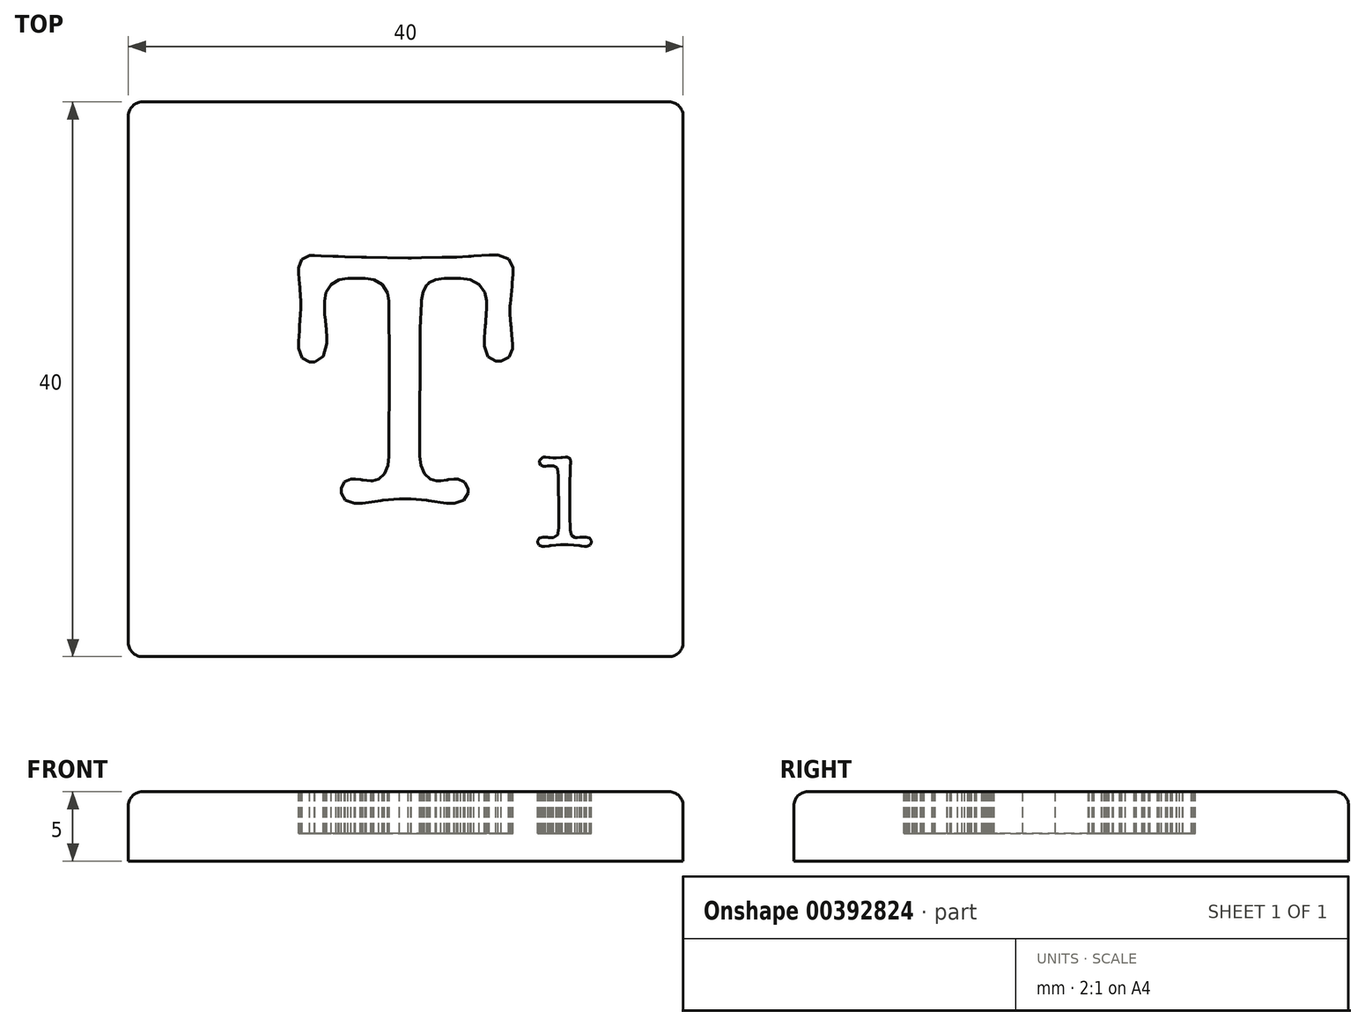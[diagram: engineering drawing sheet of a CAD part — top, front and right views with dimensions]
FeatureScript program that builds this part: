
annotation { "Feature Type Name" : "Feature", "Feature Type Description" : "" }
export const myFeature = defineFeature(function(context is Context, id is Id, definition is map)
    precondition{}
    {
        {
            var Q0;
            Q0=qCreatedBy(makeId("Top.planeOp"),FACE);
            var sketch = newSketch(context, id + "F0", { "sketchPlane" : qUnion([Q0])});
            skLineSegment(sketch, "E0.bottom", {"start": v(20, -20) * mm, "end": v(-20, -20) * mm});
            skLineSegment(sketch, "E0.top", {"start": v(20, 20) * mm, "end": v(-20, 20) * mm});
            skLineSegment(sketch, "E0.left", {"start": v(20, -20) * mm, "end": v(20, 20) * mm});
            skLineSegment(sketch, "E0.right", {"start": v(-20, -20) * mm, "end": v(-20, 20) * mm});
            skPoint(sketch, "E0.middle", {"position": v(0, 0) * mm});
            skSolve(sketch);
        }
        {
            var Q0;
            Q0=makeQuery(id+"F0.imprint","IMPRINT",FACE,{"disambiguationData":[TD([[makeQuery(id+"F0.imprint","IMPRINT",EDGE,{"derivedFrom":sQuery(id+"F0.wireOp",EDGE,"E0.bottom")}),-1.0]])]});
            extrude(context, id + "F1", {"entities" : qUnion([Q0]), "flatOperationType" : FlatOperationType.REMOVE, "offsetDistance" : 25 * mm, "depth" : -5 * mm, "domain" : OperationDomain.MODEL});
        }
        {
            var Q0;
            Q0=makeQuery(id+"F1.opExtrude","CAP_FACE",FACE,{"disambiguationData":[OSD([sQuery(id+"F0.wireOp",EDGE,"E0.bottom"),sQuery(id+"F0.wireOp",EDGE,"E0.top"),sQuery(id+"F0.wireOp",EDGE,"E0.left"),sQuery(id+"F0.wireOp",EDGE,"E0.right")])],"isStart":true});
            var Q1;
            Q1=makeQuery(id+"F1.opExtrude","SWEPT_EDGE",EDGE,{"disambiguationData":[OSD([sQuery(id+"F0.wireOp",EDGE,"E0.top"),sQuery(id+"F0.wireOp",EDGE,"E0.right")])]});
            var Q2;
            Q2=makeQuery(id+"F1.opExtrude","SWEPT_EDGE",EDGE,{"disambiguationData":[OSD([sQuery(id+"F0.wireOp",EDGE,"E0.top"),sQuery(id+"F0.wireOp",EDGE,"E0.left")])]});
            var Q3;
            Q3=makeQuery(id+"F1.opExtrude","SWEPT_EDGE",EDGE,{"disambiguationData":[OSD([sQuery(id+"F0.wireOp",EDGE,"E0.bottom"),sQuery(id+"F0.wireOp",EDGE,"E0.right")])]});
            var Q4;
            Q4=makeQuery(id+"F1.opExtrude","SWEPT_EDGE",EDGE,{"disambiguationData":[OSD([sQuery(id+"F0.wireOp",EDGE,"E0.bottom"),sQuery(id+"F0.wireOp",EDGE,"E0.left")])]});
            fillet(context, id + "F2", {"entities" : qUnion([Q0, Q1, Q2, Q3, Q4]), "radius" : 1 * mm, "tangentPropagation" : true, "allowEdgeOverflow" : false});
        }
        {
            var Q0;
            Q0=qCreatedBy(makeId("Top.planeOp"),FACE);
            var sketch = newSketch(context, id + "F3", { "sketchPlane" : qUnion([Q0])});
            skLineSegment(sketch, "E1", {"start": v(1.02, -5.33) * mm, "end": v(1.02, -5.55) * mm});
            skLineSegment(sketch, "E2", {"start": v(1.02, -5.55) * mm, "end": v(1.1, -6.2) * mm});
            skLineSegment(sketch, "E3", {"start": v(1.1, -6.2) * mm, "end": v(1.36, -6.82) * mm});
            skLineSegment(sketch, "E4", {"start": v(1.36, -6.82) * mm, "end": v(1.78, -7.2) * mm});
            skLineSegment(sketch, "E5", {"start": v(1.78, -7.2) * mm, "end": v(2.22, -7.32) * mm});
            skLineSegment(sketch, "E6", {"start": v(2.22, -7.32) * mm, "end": v(2.37, -7.32) * mm});
            skLineSegment(sketch, "E7", {"start": v(2.37, -7.32) * mm, "end": v(2.53, -7.32) * mm});
            skLineSegment(sketch, "E8", {"start": v(2.53, -7.32) * mm, "end": v(2.93, -7.26) * mm});
            skLineSegment(sketch, "E9", {"start": v(2.93, -7.26) * mm, "end": v(3, -7.25) * mm});
            skLineSegment(sketch, "E10", {"start": v(3, -7.25) * mm, "end": v(3.07, -7.24) * mm});
            skLineSegment(sketch, "E11", {"start": v(3.07, -7.24) * mm, "end": v(3.5, -7.18) * mm});
            skLineSegment(sketch, "E12", {"start": v(3.5, -7.18) * mm, "end": v(3.64, -7.18) * mm});
            skLineSegment(sketch, "E13", {"start": v(3.64, -7.18) * mm, "end": v(3.79, -7.18) * mm});
            skLineSegment(sketch, "E14", {"start": v(3.79, -7.18) * mm, "end": v(4.2, -7.4) * mm});
            skLineSegment(sketch, "E15", {"start": v(4.2, -7.4) * mm, "end": v(4.23, -7.43) * mm});
            skLineSegment(sketch, "E16", {"start": v(4.23, -7.43) * mm, "end": v(4.27, -7.48) * mm});
            skLineSegment(sketch, "E17", {"start": v(4.27, -7.48) * mm, "end": v(4.49, -7.9) * mm});
            skLineSegment(sketch, "E18", {"start": v(4.49, -7.9) * mm, "end": v(4.49, -8.03) * mm});
            skLineSegment(sketch, "E19", {"start": v(4.49, -8.03) * mm, "end": v(4.49, -8.2) * mm});
            skLineSegment(sketch, "E20", {"start": v(4.49, -8.2) * mm, "end": v(4.19, -8.72) * mm});
            skLineSegment(sketch, "E21", {"start": v(4.19, -8.72) * mm, "end": v(3.52, -8.96) * mm});
            skLineSegment(sketch, "E22", {"start": v(3.52, -8.96) * mm, "end": v(3.3, -8.96) * mm});
            skLineSegment(sketch, "E23", {"start": v(3.3, -8.96) * mm, "end": v(3.14, -8.96) * mm});
            skLineSegment(sketch, "E24", {"start": v(3.14, -8.96) * mm, "end": v(3.11, -8.95) * mm});
            skLineSegment(sketch, "E25", {"start": v(3.11, -8.95) * mm, "end": v(3, -8.93) * mm});
            skLineSegment(sketch, "E26", {"start": v(3, -8.93) * mm, "end": v(2.95, -8.93) * mm});
            skLineSegment(sketch, "E27", {"start": v(2.95, -8.93) * mm, "end": v(1.65, -8.74) * mm});
            skLineSegment(sketch, "E28", {"start": v(1.65, -8.74) * mm, "end": v(1.53, -8.73) * mm});
            skLineSegment(sketch, "E29", {"start": v(1.53, -8.73) * mm, "end": v(0.37, -8.64) * mm});
            skLineSegment(sketch, "E30", {"start": v(0.37, -8.64) * mm, "end": v(-0.01, -8.64) * mm});
            skLineSegment(sketch, "E31", {"start": v(-0.01, -8.64) * mm, "end": v(-0.46, -8.64) * mm});
            skLineSegment(sketch, "E32", {"start": v(-0.46, -8.64) * mm, "end": v(-1.66, -8.73) * mm});
            skLineSegment(sketch, "E33", {"start": v(-1.66, -8.73) * mm, "end": v(-1.79, -8.74) * mm});
            skLineSegment(sketch, "E34", {"start": v(-1.79, -8.74) * mm, "end": v(-3.1, -8.93) * mm});
            skLineSegment(sketch, "E35", {"start": v(-3.1, -8.93) * mm, "end": v(-3.16, -8.93) * mm});
            skLineSegment(sketch, "E36", {"start": v(-3.16, -8.93) * mm, "end": v(-3.28, -8.95) * mm});
            skLineSegment(sketch, "E37", {"start": v(-3.28, -8.95) * mm, "end": v(-3.3, -8.96) * mm});
            skLineSegment(sketch, "E38", {"start": v(-3.3, -8.96) * mm, "end": v(-3.48, -8.96) * mm});
            skLineSegment(sketch, "E39", {"start": v(-3.48, -8.96) * mm, "end": v(-3.7, -8.96) * mm});
            skLineSegment(sketch, "E40", {"start": v(-3.7, -8.96) * mm, "end": v(-4.35, -8.72) * mm});
            skLineSegment(sketch, "E41", {"start": v(-4.35, -8.72) * mm, "end": v(-4.64, -8.2) * mm});
            skLineSegment(sketch, "E42", {"start": v(-4.64, -8.2) * mm, "end": v(-4.64, -8.03) * mm});
            skLineSegment(sketch, "E43", {"start": v(-4.64, -8.03) * mm, "end": v(-4.64, -7.87) * mm});
            skLineSegment(sketch, "E44", {"start": v(-4.64, -7.87) * mm, "end": v(-4.43, -7.4) * mm});
            skLineSegment(sketch, "E45", {"start": v(-4.43, -7.4) * mm, "end": v(-3.96, -7.18) * mm});
            skLineSegment(sketch, "E46", {"start": v(-3.96, -7.18) * mm, "end": v(-3.8, -7.18) * mm});
            skLineSegment(sketch, "E47", {"start": v(-3.8, -7.18) * mm, "end": v(-3.64, -7.18) * mm});
            skLineSegment(sketch, "E48", {"start": v(-3.64, -7.18) * mm, "end": v(-3.23, -7.24) * mm});
            skLineSegment(sketch, "E49", {"start": v(-3.23, -7.24) * mm, "end": v(-3.16, -7.25) * mm});
            skLineSegment(sketch, "E50", {"start": v(-3.16, -7.25) * mm, "end": v(-3.1, -7.26) * mm});
            skLineSegment(sketch, "E51", {"start": v(-3.1, -7.26) * mm, "end": v(-2.53, -7.32) * mm});
            skLineSegment(sketch, "E52", {"start": v(-2.53, -7.32) * mm, "end": v(-2.38, -7.32) * mm});
            skLineSegment(sketch, "E53", {"start": v(-2.38, -7.32) * mm, "end": v(-1.95, -7.2) * mm});
            skLineSegment(sketch, "E54", {"start": v(-1.95, -7.2) * mm, "end": v(-1.53, -6.82) * mm});
            skLineSegment(sketch, "E55", {"start": v(-1.53, -6.82) * mm, "end": v(-1.29, -6.2) * mm});
            skLineSegment(sketch, "E56", {"start": v(-1.29, -6.2) * mm, "end": v(-1.2, -5.55) * mm});
            skLineSegment(sketch, "E57", {"start": v(-1.2, -5.55) * mm, "end": v(-1.2, -5.33) * mm});
            skLineSegment(sketch, "E58", {"start": v(-1.2, -5.33) * mm, "end": v(-1.2, -3.48) * mm});
            skLineSegment(sketch, "E59", {"start": v(-1.2, -3.48) * mm, "end": v(-1.18, -1.15) * mm});
            skLineSegment(sketch, "E60", {"start": v(-1.18, -1.15) * mm, "end": v(-1.18, 1.1) * mm});
            skLineSegment(sketch, "E61", {"start": v(-1.18, 1.1) * mm, "end": v(-1.2, 5.41) * mm});
            skLineSegment(sketch, "E62", {"start": v(-1.2, 5.41) * mm, "end": v(-1.2, 5.62) * mm});
            skLineSegment(sketch, "E63", {"start": v(-1.2, 5.62) * mm, "end": v(-1.32, 6.23) * mm});
            skLineSegment(sketch, "E64", {"start": v(-1.32, 6.23) * mm, "end": v(-1.69, 6.82) * mm});
            skLineSegment(sketch, "E65", {"start": v(-1.69, 6.82) * mm, "end": v(-2.3, 7.17) * mm});
            skLineSegment(sketch, "E66", {"start": v(-2.3, 7.17) * mm, "end": v(-2.92, 7.29) * mm});
            skLineSegment(sketch, "E67", {"start": v(-2.92, 7.29) * mm, "end": v(-3.14, 7.29) * mm});
            skLineSegment(sketch, "E68", {"start": v(-3.14, 7.29) * mm, "end": v(-3.95, 7.29) * mm});
            skLineSegment(sketch, "E69", {"start": v(-3.95, 7.29) * mm, "end": v(-4.16, 7.29) * mm});
            skLineSegment(sketch, "E70", {"start": v(-4.16, 7.29) * mm, "end": v(-4.8, 7.17) * mm});
            skLineSegment(sketch, "E71", {"start": v(-4.8, 7.17) * mm, "end": v(-5.39, 6.83) * mm});
            skLineSegment(sketch, "E72", {"start": v(-5.39, 6.83) * mm, "end": v(-5.74, 6.25) * mm});
            skLineSegment(sketch, "E73", {"start": v(-5.74, 6.25) * mm, "end": v(-5.86, 5.64) * mm});
            skLineSegment(sketch, "E74", {"start": v(-5.86, 5.64) * mm, "end": v(-5.86, 5.44) * mm});
            skLineSegment(sketch, "E75", {"start": v(-5.86, 5.44) * mm, "end": v(-5.86, 5.21) * mm});
            skLineSegment(sketch, "E76", {"start": v(-5.86, 5.21) * mm, "end": v(-5.84, 4.58) * mm});
            skLineSegment(sketch, "E77", {"start": v(-5.84, 4.58) * mm, "end": v(-5.83, 4.54) * mm});
            skLineSegment(sketch, "E78", {"start": v(-5.83, 4.54) * mm, "end": v(-5.73, 3.56) * mm});
            skLineSegment(sketch, "E79", {"start": v(-5.73, 3.56) * mm, "end": v(-5.72, 3.52) * mm});
            skLineSegment(sketch, "E80", {"start": v(-5.72, 3.52) * mm, "end": v(-5.7, 3.05) * mm});
            skLineSegment(sketch, "E81", {"start": v(-5.7, 3.05) * mm, "end": v(-5.7, 2.9) * mm});
            skLineSegment(sketch, "E82", {"start": v(-5.7, 2.9) * mm, "end": v(-5.7, 2.59) * mm});
            skLineSegment(sketch, "E83", {"start": v(-5.7, 2.59) * mm, "end": v(-5.96, 1.65) * mm});
            skLineSegment(sketch, "E84", {"start": v(-5.96, 1.65) * mm, "end": v(-6.54, 1.23) * mm});
            skLineSegment(sketch, "E85", {"start": v(-6.54, 1.23) * mm, "end": v(-6.73, 1.23) * mm});
            skLineSegment(sketch, "E86", {"start": v(-6.73, 1.23) * mm, "end": v(-6.92, 1.23) * mm});
            skLineSegment(sketch, "E87", {"start": v(-6.92, 1.23) * mm, "end": v(-7.47, 1.54) * mm});
            skLineSegment(sketch, "E88", {"start": v(-7.47, 1.54) * mm, "end": v(-7.71, 2.22) * mm});
            skLineSegment(sketch, "E89", {"start": v(-7.71, 2.22) * mm, "end": v(-7.71, 2.45) * mm});
            skLineSegment(sketch, "E90", {"start": v(-7.71, 2.45) * mm, "end": v(-7.71, 2.75) * mm});
            skLineSegment(sketch, "E91", {"start": v(-7.71, 2.75) * mm, "end": v(-7.67, 3.5) * mm});
            skLineSegment(sketch, "E92", {"start": v(-7.67, 3.5) * mm, "end": v(-7.66, 3.64) * mm});
            skLineSegment(sketch, "E93", {"start": v(-7.66, 3.64) * mm, "end": v(-7.65, 3.85) * mm});
            skLineSegment(sketch, "E94", {"start": v(-7.65, 3.85) * mm, "end": v(-7.6, 4.68) * mm});
            skLineSegment(sketch, "E95", {"start": v(-7.6, 4.68) * mm, "end": v(-7.58, 5.1) * mm});
            skLineSegment(sketch, "E96", {"start": v(-7.58, 5.1) * mm, "end": v(-7.58, 5.25) * mm});
            skLineSegment(sketch, "E97", {"start": v(-7.58, 5.25) * mm, "end": v(-7.58, 5.6) * mm});
            skLineSegment(sketch, "E98", {"start": v(-7.58, 5.6) * mm, "end": v(-7.62, 6.5) * mm});
            skLineSegment(sketch, "E99", {"start": v(-7.62, 6.5) * mm, "end": v(-7.63, 6.63) * mm});
            skLineSegment(sketch, "E100", {"start": v(-7.63, 6.63) * mm, "end": v(-7.65, 6.86) * mm});
            skLineSegment(sketch, "E101", {"start": v(-7.65, 6.86) * mm, "end": v(-7.71, 7.63) * mm});
            skLineSegment(sketch, "E102", {"start": v(-7.71, 7.63) * mm, "end": v(-7.74, 7.82) * mm});
            skLineSegment(sketch, "E103", {"start": v(-7.74, 7.82) * mm, "end": v(-7.74, 8.03) * mm});
            skLineSegment(sketch, "E104", {"start": v(-7.74, 8.03) * mm, "end": v(-7.49, 8.65) * mm});
            skLineSegment(sketch, "E105", {"start": v(-7.49, 8.65) * mm, "end": v(-6.92, 8.93) * mm});
            skLineSegment(sketch, "E106", {"start": v(-6.92, 8.93) * mm, "end": v(-6.73, 8.93) * mm});
            skLineSegment(sketch, "E107", {"start": v(-6.73, 8.93) * mm, "end": v(-6.58, 8.93) * mm});
            skLineSegment(sketch, "E108", {"start": v(-6.58, 8.93) * mm, "end": v(-6.12, 8.91) * mm});
            skLineSegment(sketch, "E109", {"start": v(-6.12, 8.91) * mm, "end": v(-5.24, 8.86) * mm});
            skLineSegment(sketch, "E110", {"start": v(-5.24, 8.86) * mm, "end": v(-5.01, 8.85) * mm});
            skLineSegment(sketch, "E111", {"start": v(-5.01, 8.85) * mm, "end": v(-4.86, 8.85) * mm});
            skLineSegment(sketch, "E112", {"start": v(-4.86, 8.85) * mm, "end": v(-4.4, 8.84) * mm});
            skLineSegment(sketch, "E113", {"start": v(-4.4, 8.84) * mm, "end": v(-3.18, 8.8) * mm});
            skLineSegment(sketch, "E114", {"start": v(-3.18, 8.8) * mm, "end": v(-2.84, 8.8) * mm});
            skLineSegment(sketch, "E115", {"start": v(-2.84, 8.8) * mm, "end": v(0.17, 8.75) * mm});
            skLineSegment(sketch, "E116", {"start": v(0.17, 8.75) * mm, "end": v(0.41, 8.75) * mm});
            skLineSegment(sketch, "E117", {"start": v(0.41, 8.75) * mm, "end": v(1.14, 8.76) * mm});
            skLineSegment(sketch, "E118", {"start": v(1.14, 8.76) * mm, "end": v(2.62, 8.79) * mm});
            skLineSegment(sketch, "E119", {"start": v(2.62, 8.79) * mm, "end": v(3, 8.8) * mm});
            skLineSegment(sketch, "E120", {"start": v(3, 8.8) * mm, "end": v(3.17, 8.8) * mm});
            skLineSegment(sketch, "E121", {"start": v(3.17, 8.8) * mm, "end": v(3.68, 8.82) * mm});
            skLineSegment(sketch, "E122", {"start": v(3.68, 8.82) * mm, "end": v(4.52, 8.86) * mm});
            skLineSegment(sketch, "E123", {"start": v(4.52, 8.86) * mm, "end": v(4.72, 8.88) * mm});
            skLineSegment(sketch, "E124", {"start": v(4.72, 8.88) * mm, "end": v(4.9, 8.9) * mm});
            skLineSegment(sketch, "E125", {"start": v(4.9, 8.9) * mm, "end": v(6.04, 8.96) * mm});
            skLineSegment(sketch, "E126", {"start": v(6.04, 8.96) * mm, "end": v(6.42, 8.96) * mm});
            skLineSegment(sketch, "E127", {"start": v(6.42, 8.96) * mm, "end": v(6.66, 8.96) * mm});
            skLineSegment(sketch, "E128", {"start": v(6.66, 8.96) * mm, "end": v(7.4, 8.69) * mm});
            skLineSegment(sketch, "E129", {"start": v(7.4, 8.69) * mm, "end": v(7.74, 8.08) * mm});
            skLineSegment(sketch, "E130", {"start": v(7.74, 8.08) * mm, "end": v(7.74, 7.87) * mm});
            skLineSegment(sketch, "E131", {"start": v(7.74, 7.87) * mm, "end": v(7.74, 7.82) * mm});
            skLineSegment(sketch, "E132", {"start": v(7.74, 7.82) * mm, "end": v(7.74, 7.58) * mm});
            skLineSegment(sketch, "E133", {"start": v(7.74, 7.58) * mm, "end": v(7.68, 6.96) * mm});
            skLineSegment(sketch, "E134", {"start": v(7.68, 6.96) * mm, "end": v(7.67, 6.84) * mm});
            skLineSegment(sketch, "E135", {"start": v(7.67, 6.84) * mm, "end": v(7.66, 6.72) * mm});
            skLineSegment(sketch, "E136", {"start": v(7.66, 6.72) * mm, "end": v(7.54, 5.44) * mm});
            skLineSegment(sketch, "E137", {"start": v(7.54, 5.44) * mm, "end": v(7.53, 5.3) * mm});
            skLineSegment(sketch, "E138", {"start": v(7.53, 5.3) * mm, "end": v(7.53, 5.01) * mm});
            skLineSegment(sketch, "E139", {"start": v(7.53, 5.01) * mm, "end": v(7.53, 4.7) * mm});
            skLineSegment(sketch, "E140", {"start": v(7.53, 4.7) * mm, "end": v(7.6, 3.91) * mm});
            skLineSegment(sketch, "E141", {"start": v(7.6, 3.91) * mm, "end": v(7.6, 3.77) * mm});
            skLineSegment(sketch, "E142", {"start": v(7.6, 3.77) * mm, "end": v(7.62, 3.59) * mm});
            skLineSegment(sketch, "E143", {"start": v(7.62, 3.59) * mm, "end": v(7.69, 2.87) * mm});
            skLineSegment(sketch, "E144", {"start": v(7.69, 2.87) * mm, "end": v(7.71, 2.51) * mm});
            skLineSegment(sketch, "E145", {"start": v(7.71, 2.51) * mm, "end": v(7.71, 2.4) * mm});
            skLineSegment(sketch, "E146", {"start": v(7.71, 2.4) * mm, "end": v(7.71, 2.2) * mm});
            skLineSegment(sketch, "E147", {"start": v(7.71, 2.2) * mm, "end": v(7.45, 1.58) * mm});
            skLineSegment(sketch, "E148", {"start": v(7.45, 1.58) * mm, "end": v(6.87, 1.31) * mm});
            skLineSegment(sketch, "E149", {"start": v(6.87, 1.31) * mm, "end": v(6.68, 1.31) * mm});
            skLineSegment(sketch, "E150", {"start": v(6.68, 1.31) * mm, "end": v(6.5, 1.31) * mm});
            skLineSegment(sketch, "E151", {"start": v(6.5, 1.31) * mm, "end": v(5.93, 1.64) * mm});
            skLineSegment(sketch, "E152", {"start": v(5.93, 1.64) * mm, "end": v(5.68, 2.39) * mm});
            skLineSegment(sketch, "E153", {"start": v(5.68, 2.39) * mm, "end": v(5.68, 2.63) * mm});
            skLineSegment(sketch, "E154", {"start": v(5.68, 2.63) * mm, "end": v(5.68, 2.99) * mm});
            skLineSegment(sketch, "E155", {"start": v(5.68, 2.99) * mm, "end": v(5.74, 3.9) * mm});
            skLineSegment(sketch, "E156", {"start": v(5.74, 3.9) * mm, "end": v(5.75, 4.05) * mm});
            skLineSegment(sketch, "E157", {"start": v(5.75, 4.05) * mm, "end": v(5.77, 4.2) * mm});
            skLineSegment(sketch, "E158", {"start": v(5.77, 4.2) * mm, "end": v(5.83, 5.15) * mm});
            skLineSegment(sketch, "E159", {"start": v(5.83, 5.15) * mm, "end": v(5.83, 5.46) * mm});
            skLineSegment(sketch, "E160", {"start": v(5.83, 5.46) * mm, "end": v(5.83, 5.66) * mm});
            skLineSegment(sketch, "E161", {"start": v(5.83, 5.66) * mm, "end": v(5.7, 6.26) * mm});
            skLineSegment(sketch, "E162", {"start": v(5.7, 6.26) * mm, "end": v(5.31, 6.83) * mm});
            skLineSegment(sketch, "E163", {"start": v(5.31, 6.83) * mm, "end": v(4.66, 7.18) * mm});
            skLineSegment(sketch, "E164", {"start": v(4.66, 7.18) * mm, "end": v(3.97, 7.29) * mm});
            skLineSegment(sketch, "E165", {"start": v(3.97, 7.29) * mm, "end": v(3.74, 7.29) * mm});
            skLineSegment(sketch, "E166", {"start": v(3.74, 7.29) * mm, "end": v(3, 7.29) * mm});
            skLineSegment(sketch, "E167", {"start": v(3, 7.29) * mm, "end": v(2.8, 7.29) * mm});
            skLineSegment(sketch, "E168", {"start": v(2.8, 7.29) * mm, "end": v(2.16, 7.19) * mm});
            skLineSegment(sketch, "E169", {"start": v(2.16, 7.19) * mm, "end": v(1.67, 6.95) * mm});
            skLineSegment(sketch, "E170", {"start": v(1.67, 6.95) * mm, "end": v(1.6, 6.88) * mm});
            skLineSegment(sketch, "E171", {"start": v(1.6, 6.88) * mm, "end": v(1.53, 6.81) * mm});
            skLineSegment(sketch, "E172", {"start": v(1.53, 6.81) * mm, "end": v(1.27, 6.33) * mm});
            skLineSegment(sketch, "E173", {"start": v(1.27, 6.33) * mm, "end": v(1.13, 5.68) * mm});
            skLineSegment(sketch, "E174", {"start": v(1.13, 5.68) * mm, "end": v(1.12, 5.52) * mm});
            skLineSegment(sketch, "E175", {"start": v(1.12, 5.52) * mm, "end": v(1.05, 3.66) * mm});
            skLineSegment(sketch, "E176", {"start": v(1.05, 3.66) * mm, "end": v(1.02, -5.33) * mm});
            skSolve(sketch);
        }
        {
            var Q0;
            Q0=qCreatedBy(makeId("Top.planeOp"),FACE);
            var sketch = newSketch(context, id + "F4", { "sketchPlane" : qUnion([Q0])});
            skLineSegment(sketch, "E177", {"start": v(11.05, -9.8) * mm, "end": v(11.02, -7.04) * mm});
            skLineSegment(sketch, "E178", {"start": v(11.02, -7.04) * mm, "end": v(11.02, -6.96) * mm});
            skLineSegment(sketch, "E179", {"start": v(11.02, -6.96) * mm, "end": v(10.94, -6.42) * mm});
            skLineSegment(sketch, "E180", {"start": v(10.94, -6.42) * mm, "end": v(10.92, -6.4) * mm});
            skLineSegment(sketch, "E181", {"start": v(10.92, -6.4) * mm, "end": v(10.9, -6.37) * mm});
            skLineSegment(sketch, "E182", {"start": v(10.9, -6.37) * mm, "end": v(10.65, -6.23) * mm});
            skLineSegment(sketch, "E183", {"start": v(10.65, -6.23) * mm, "end": v(10.57, -6.23) * mm});
            skLineSegment(sketch, "E184", {"start": v(10.57, -6.23) * mm, "end": v(10.5, -6.23) * mm});
            skLineSegment(sketch, "E185", {"start": v(10.5, -6.23) * mm, "end": v(10.32, -6.25) * mm});
            skLineSegment(sketch, "E186", {"start": v(10.32, -6.25) * mm, "end": v(10.29, -6.26) * mm});
            skLineSegment(sketch, "E187", {"start": v(10.29, -6.26) * mm, "end": v(10.26, -6.26) * mm});
            skLineSegment(sketch, "E188", {"start": v(10.26, -6.26) * mm, "end": v(10.07, -6.28) * mm});
            skLineSegment(sketch, "E189", {"start": v(10.07, -6.28) * mm, "end": v(10.01, -6.28) * mm});
            skLineSegment(sketch, "E190", {"start": v(10.01, -6.28) * mm, "end": v(9.94, -6.28) * mm});
            skLineSegment(sketch, "E191", {"start": v(9.94, -6.28) * mm, "end": v(9.73, -6.2) * mm});
            skLineSegment(sketch, "E192", {"start": v(9.73, -6.2) * mm, "end": v(9.64, -6.01) * mm});
            skLineSegment(sketch, "E193", {"start": v(9.64, -6.01) * mm, "end": v(9.64, -5.95) * mm});
            skLineSegment(sketch, "E194", {"start": v(9.64, -5.95) * mm, "end": v(9.64, -5.86) * mm});
            skLineSegment(sketch, "E195", {"start": v(9.64, -5.86) * mm, "end": v(9.9, -5.61) * mm});
            skLineSegment(sketch, "E196", {"start": v(9.9, -5.61) * mm, "end": v(10, -5.61) * mm});
            skLineSegment(sketch, "E197", {"start": v(10, -5.61) * mm, "end": v(10.08, -5.61) * mm});
            skLineSegment(sketch, "E198", {"start": v(10.08, -5.61) * mm, "end": v(10.31, -5.63) * mm});
            skLineSegment(sketch, "E199", {"start": v(10.31, -5.63) * mm, "end": v(10.35, -5.64) * mm});
            skLineSegment(sketch, "E200", {"start": v(10.35, -5.64) * mm, "end": v(10.4, -5.64) * mm});
            skLineSegment(sketch, "E201", {"start": v(10.4, -5.64) * mm, "end": v(10.64, -5.66) * mm});
            skLineSegment(sketch, "E202", {"start": v(10.64, -5.66) * mm, "end": v(10.73, -5.66) * mm});
            skLineSegment(sketch, "E203", {"start": v(10.73, -5.66) * mm, "end": v(10.85, -5.66) * mm});
            skLineSegment(sketch, "E204", {"start": v(10.85, -5.66) * mm, "end": v(11.2, -5.65) * mm});
            skLineSegment(sketch, "E205", {"start": v(11.2, -5.65) * mm, "end": v(11.23, -5.64) * mm});
            skLineSegment(sketch, "E206", {"start": v(11.23, -5.64) * mm, "end": v(11.28, -5.64) * mm});
            skLineSegment(sketch, "E207", {"start": v(11.28, -5.64) * mm, "end": v(11.52, -5.61) * mm});
            skLineSegment(sketch, "E208", {"start": v(11.52, -5.61) * mm, "end": v(11.6, -5.61) * mm});
            skLineSegment(sketch, "E209", {"start": v(11.6, -5.61) * mm, "end": v(11.66, -5.61) * mm});
            skLineSegment(sketch, "E210", {"start": v(11.66, -5.61) * mm, "end": v(11.84, -5.72) * mm});
            skLineSegment(sketch, "E211", {"start": v(11.84, -5.72) * mm, "end": v(11.85, -5.74) * mm});
            skLineSegment(sketch, "E212", {"start": v(11.85, -5.74) * mm, "end": v(11.86, -5.75) * mm});
            skLineSegment(sketch, "E213", {"start": v(11.86, -5.75) * mm, "end": v(11.89, -5.96) * mm});
            skLineSegment(sketch, "E214", {"start": v(11.89, -5.96) * mm, "end": v(11.89, -6.03) * mm});
            skLineSegment(sketch, "E215", {"start": v(11.89, -6.03) * mm, "end": v(11.89, -6.1) * mm});
            skLineSegment(sketch, "E216", {"start": v(11.89, -6.1) * mm, "end": v(11.88, -6.23) * mm});
            skLineSegment(sketch, "E217", {"start": v(11.88, -6.23) * mm, "end": v(11.88, -6.26) * mm});
            skLineSegment(sketch, "E218", {"start": v(11.88, -6.26) * mm, "end": v(11.87, -6.43) * mm});
            skLineSegment(sketch, "E219", {"start": v(11.87, -6.43) * mm, "end": v(11.83, -7.69) * mm});
            skLineSegment(sketch, "E220", {"start": v(11.83, -7.69) * mm, "end": v(11.83, -8.11) * mm});
            skLineSegment(sketch, "E221", {"start": v(11.83, -8.11) * mm, "end": v(11.83, -9.19) * mm});
            skLineSegment(sketch, "E222", {"start": v(11.83, -9.19) * mm, "end": v(11.84, -9.9) * mm});
            skLineSegment(sketch, "E223", {"start": v(11.84, -9.9) * mm, "end": v(11.84, -9.98) * mm});
            skLineSegment(sketch, "E224", {"start": v(11.84, -9.98) * mm, "end": v(11.85, -10.08) * mm});
            skLineSegment(sketch, "E225", {"start": v(11.85, -10.08) * mm, "end": v(11.86, -10.6) * mm});
            skLineSegment(sketch, "E226", {"start": v(11.86, -10.6) * mm, "end": v(11.86, -10.77) * mm});
            skLineSegment(sketch, "E227", {"start": v(11.86, -10.77) * mm, "end": v(11.86, -10.88) * mm});
            skLineSegment(sketch, "E228", {"start": v(11.86, -10.88) * mm, "end": v(11.98, -11.26) * mm});
            skLineSegment(sketch, "E229", {"start": v(11.98, -11.26) * mm, "end": v(12.22, -11.42) * mm});
            skLineSegment(sketch, "E230", {"start": v(12.22, -11.42) * mm, "end": v(12.3, -11.42) * mm});
            skLineSegment(sketch, "E231", {"start": v(12.3, -11.42) * mm, "end": v(12.38, -11.42) * mm});
            skLineSegment(sketch, "E232", {"start": v(12.38, -11.42) * mm, "end": v(12.58, -11.4) * mm});
            skLineSegment(sketch, "E233", {"start": v(12.58, -11.4) * mm, "end": v(12.61, -11.4) * mm});
            skLineSegment(sketch, "E234", {"start": v(12.61, -11.4) * mm, "end": v(12.65, -11.4) * mm});
            skLineSegment(sketch, "E235", {"start": v(12.65, -11.4) * mm, "end": v(12.93, -11.38) * mm});
            skLineSegment(sketch, "E236", {"start": v(12.93, -11.38) * mm, "end": v(13.01, -11.38) * mm});
            skLineSegment(sketch, "E237", {"start": v(13.01, -11.38) * mm, "end": v(13.27, -11.46) * mm});
            skLineSegment(sketch, "E238", {"start": v(13.27, -11.46) * mm, "end": v(13.39, -11.65) * mm});
            skLineSegment(sketch, "E239", {"start": v(13.39, -11.65) * mm, "end": v(13.39, -11.71) * mm});
            skLineSegment(sketch, "E240", {"start": v(13.39, -11.71) * mm, "end": v(13.39, -11.77) * mm});
            skLineSegment(sketch, "E241", {"start": v(13.39, -11.77) * mm, "end": v(13.28, -11.96) * mm});
            skLineSegment(sketch, "E242", {"start": v(13.28, -11.96) * mm, "end": v(13.04, -12.04) * mm});
            skLineSegment(sketch, "E243", {"start": v(13.04, -12.04) * mm, "end": v(12.97, -12.04) * mm});
            skLineSegment(sketch, "E244", {"start": v(12.97, -12.04) * mm, "end": v(12.89, -12.04) * mm});
            skLineSegment(sketch, "E245", {"start": v(12.89, -12.04) * mm, "end": v(12.68, -12.03) * mm});
            skLineSegment(sketch, "E246", {"start": v(12.68, -12.03) * mm, "end": v(12.66, -12.03) * mm});
            skLineSegment(sketch, "E247", {"start": v(12.66, -12.03) * mm, "end": v(12.53, -12) * mm});
            skLineSegment(sketch, "E248", {"start": v(12.53, -12) * mm, "end": v(11.71, -11.92) * mm});
            skLineSegment(sketch, "E249", {"start": v(11.71, -11.92) * mm, "end": v(11.44, -11.92) * mm});
            skLineSegment(sketch, "E250", {"start": v(11.44, -11.92) * mm, "end": v(11.18, -11.92) * mm});
            skLineSegment(sketch, "E251", {"start": v(11.18, -11.92) * mm, "end": v(10.51, -12) * mm});
            skLineSegment(sketch, "E252", {"start": v(10.51, -12) * mm, "end": v(10.41, -12) * mm});
            skLineSegment(sketch, "E253", {"start": v(10.41, -12) * mm, "end": v(10.36, -12.01) * mm});
            skLineSegment(sketch, "E254", {"start": v(10.36, -12.01) * mm, "end": v(10.03, -12.05) * mm});
            skLineSegment(sketch, "E255", {"start": v(10.03, -12.05) * mm, "end": v(9.93, -12.05) * mm});
            skLineSegment(sketch, "E256", {"start": v(9.93, -12.05) * mm, "end": v(9.85, -12.05) * mm});
            skLineSegment(sketch, "E257", {"start": v(9.85, -12.05) * mm, "end": v(9.62, -11.97) * mm});
            skLineSegment(sketch, "E258", {"start": v(9.62, -11.97) * mm, "end": v(9.52, -11.77) * mm});
            skLineSegment(sketch, "E259", {"start": v(9.52, -11.77) * mm, "end": v(9.52, -11.71) * mm});
            skLineSegment(sketch, "E260", {"start": v(9.52, -11.71) * mm, "end": v(9.52, -11.65) * mm});
            skLineSegment(sketch, "E261", {"start": v(9.52, -11.65) * mm, "end": v(9.63, -11.46) * mm});
            skLineSegment(sketch, "E262", {"start": v(9.63, -11.46) * mm, "end": v(9.9, -11.38) * mm});
            skLineSegment(sketch, "E263", {"start": v(9.9, -11.38) * mm, "end": v(9.99, -11.38) * mm});
            skLineSegment(sketch, "E264", {"start": v(9.99, -11.38) * mm, "end": v(10.06, -11.38) * mm});
            skLineSegment(sketch, "E265", {"start": v(10.06, -11.38) * mm, "end": v(10.25, -11.4) * mm});
            skLineSegment(sketch, "E266", {"start": v(10.25, -11.4) * mm, "end": v(10.28, -11.4) * mm});
            skLineSegment(sketch, "E267", {"start": v(10.28, -11.4) * mm, "end": v(10.32, -11.4) * mm});
            skLineSegment(sketch, "E268", {"start": v(10.32, -11.4) * mm, "end": v(10.5, -11.42) * mm});
            skLineSegment(sketch, "E269", {"start": v(10.5, -11.42) * mm, "end": v(10.57, -11.42) * mm});
            skLineSegment(sketch, "E270", {"start": v(10.57, -11.42) * mm, "end": v(10.67, -11.42) * mm});
            skLineSegment(sketch, "E271", {"start": v(10.67, -11.42) * mm, "end": v(10.96, -11.2) * mm});
            skLineSegment(sketch, "E272", {"start": v(10.96, -11.2) * mm, "end": v(10.98, -11.16) * mm});
            skLineSegment(sketch, "E273", {"start": v(10.98, -11.16) * mm, "end": v(10.99, -11.12) * mm});
            skLineSegment(sketch, "E274", {"start": v(10.99, -11.12) * mm, "end": v(11.03, -10.7) * mm});
            skLineSegment(sketch, "E275", {"start": v(11.03, -10.7) * mm, "end": v(11.05, -10.03) * mm});
            skLineSegment(sketch, "E276", {"start": v(11.05, -10.03) * mm, "end": v(11.05, -9.8) * mm});
            skSolve(sketch);
        }
        {
            var Q0;
            Q0=qSketchRegion(id+"F3",true);
            var Q1;
            Q1=qSketchRegion(id+"F4",true);
            extrude(context, id + "F5", {"entities" : qUnion([Q0, Q1]), "flatOperationType" : FlatOperationType.REMOVE, "offsetDistance" : 25 * mm, "depth" : -3 * mm, "domain" : OperationDomain.MODEL});
        }
    });
